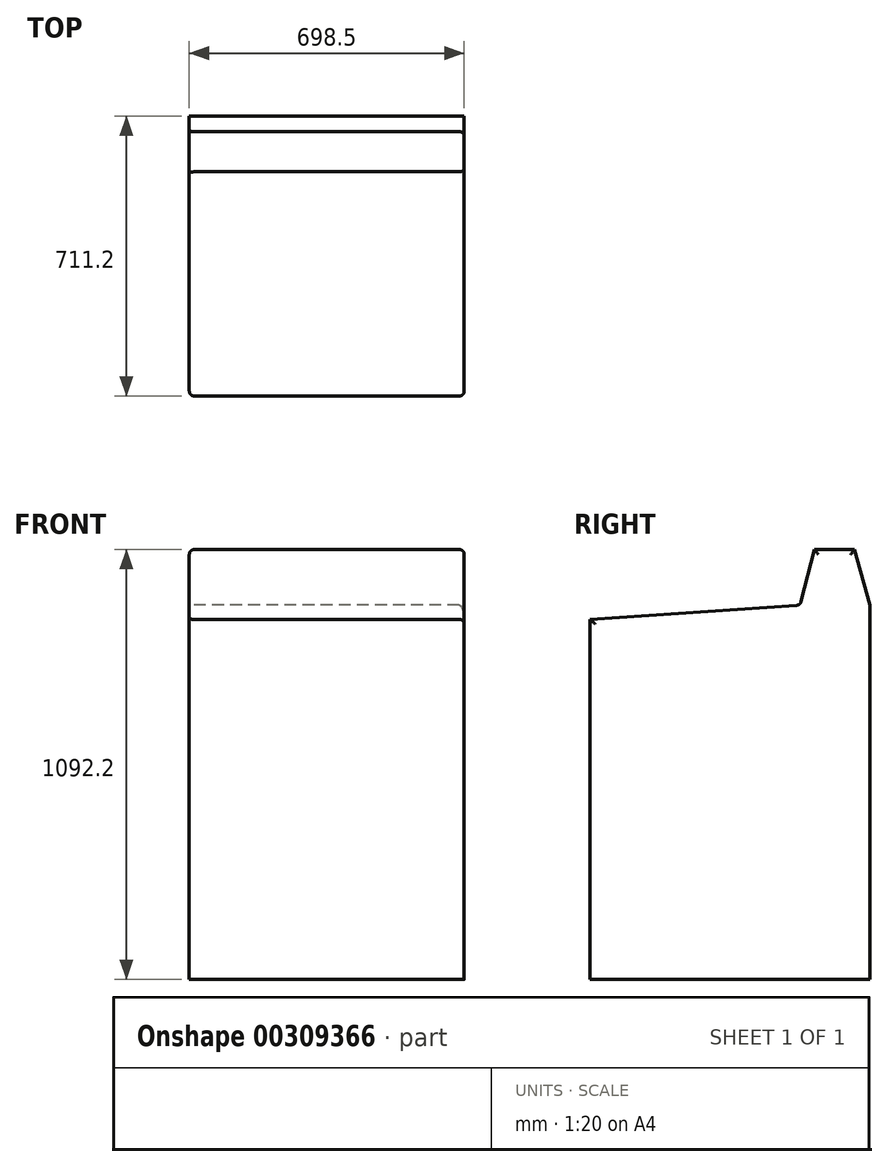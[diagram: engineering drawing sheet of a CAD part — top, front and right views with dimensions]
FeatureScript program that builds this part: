
annotation { "Feature Type Name" : "Feature", "Feature Type Description" : "" }
export const myFeature = defineFeature(function(context is Context, id is Id, definition is map)
    precondition{}
    {
        {
            var Q0;
            Q0=qCreatedBy(makeId("Top.planeOp"),FACE);
            var sketch = newSketch(context, id + "F0", { "sketchPlane" : qUnion([Q0])});
            skLineSegment(sketch, "E0.bottom", {"start": v(0, 0) * mm, "end": v(698.5, 0) * mm});
            skLineSegment(sketch, "E0.top", {"start": v(0, -711.2) * mm, "end": v(698.5, -711.2) * mm});
            skLineSegment(sketch, "E0.left", {"start": v(0, 0) * mm, "end": v(0, -711.2) * mm});
            skLineSegment(sketch, "E0.right", {"start": v(698.5, 0) * mm, "end": v(698.5, -711.2) * mm});
            skSolve(sketch);
        }
        {
            var Q0;
            Q0 = qSketchRegion(id + "F0", true);
            extrude(context, id + "F1", {"entities" : qUnion([Q0]), "depth" : 1092.2 * mm});
        }
        {
            var Q0;
            Q0=makeQuery(id+"F1.opExtrude","SWEPT_FACE",FACE,{"disambiguationData":[OSD([sQuery(id+"F0.wireOp",EDGE,"E0.left")])]});
            var sketch = newSketch(context, id + "F2", { "sketchPlane" : qUnion([Q0])});
            skLineSegment(sketch, "E1", {"start": v(0, 950.97) * mm, "end": v(39.62, 1092.2) * mm});
            skLineSegment(sketch, "E2", {"start": v(39.62, 1092.2) * mm, "end": v(141.55, 1092.2) * mm});
            skLineSegment(sketch, "E3", {"start": v(141.55, 1092.2) * mm, "end": v(177.52, 950.97) * mm});
            skLineSegment(sketch, "E4", {"start": v(177.52, 950.97) * mm, "end": v(711.2, 915) * mm});
            skSolve(sketch);
        }
        {
            var Q0;
            Q0 = qSketchRegion(id + "F2", true);
            var Q1;
            {var subQ0=sQuery(id+"F2.wireOp",EDGE,"E3");Q1=makeQuery(id+"F2.imprint","IMPRINT",FACE,{"disambiguationData":[TD([[makeQuery(id+"F2.imprint","IMPRINT",EDGE,{"derivedFrom":subQ0}),1.0]])]});}
            var Q2;
            {var subQ0=sQuery(id+"F2.wireOp",EDGE,"E1");Q2=makeQuery(id+"F2.imprint","IMPRINT",FACE,{"disambiguationData":[TD([[makeQuery(id+"F2.imprint","IMPRINT",EDGE,{"derivedFrom":subQ0}),1.0]])]});}
            extrude(context, id + "F3", {"entities" : qUnion([Q0, Q1, Q2]), "operationType" : NewBodyOperationType.REMOVE, "endBound" : BoundingType.THROUGH_ALL, "oppositeDirection" : true, "depth" : 25.4 * mm});
        }
        {
            var Q0;
            Q0=makeQuery(id+"F1.opExtrude","SWEPT_EDGE",EDGE,{"disambiguationData":[OSD([sQuery(id+"F0.wireOp",EDGE,"E0.top"),sQuery(id+"F0.wireOp",EDGE,"E0.left")])]});
            var Q1;
            Q1=makeQuery(id+"F1.opExtrude","SWEPT_EDGE",EDGE,{"disambiguationData":[OSD([sQuery(id+"F0.wireOp",EDGE,"E0.top"),sQuery(id+"F0.wireOp",EDGE,"E0.right")])]});
            var Q2;
            Q2=makeQuery(id+"F3.boolean.opBoolean","COPY",EDGE,{"derivedFrom":makeQuery(id+"F3.opExtrude","SWEPT_EDGE",EDGE,{"disambiguationData":[OSD([sQuery(id+"F0.wireOp",EDGE,"E0.top"),sQuery(id+"F0.wireOp",EDGE,"E0.left"),sQuery(id+"F2.wireOp",EDGE,"E4")])]})});
            var Q3;
            Q3=makeQuery(id+"F3.boolean.opBoolean","COPY",EDGE,{"derivedFrom":makeQuery(id+"F3.opExtrude","CAP_EDGE",EDGE,{"disambiguationData":[OSD([sQuery(id+"F2.wireOp",EDGE,"E4")])],"isStart":true})});
            var Q4;
            Q4=makeQuery(id+"F3.boolean.opBoolean","INTERSECT",EDGE,{"derivedFrom":[makeQuery(id+"F1.opExtrude","SWEPT_FACE",FACE,{"disambiguationData":[OSD([sQuery(id+"F0.wireOp",EDGE,"E0.right")])]}),makeQuery(id+"F3.opExtrude","SWEPT_FACE",FACE,{"disambiguationData":[OSD([sQuery(id+"F2.wireOp",EDGE,"E4")])]})]});
            var Q5;
            Q5=makeQuery(id+"F3.boolean.opBoolean","COPY",EDGE,{"derivedFrom":makeQuery(id+"F3.opExtrude","SWEPT_EDGE",EDGE,{"disambiguationData":[OSD([sQuery(id+"F2.wireOp",EDGE,"E3"),sQuery(id+"F2.wireOp",EDGE,"E4")])]})});
            var Q6;
            Q6=makeQuery(id+"F3.boolean.opBoolean","COPY",EDGE,{"derivedFrom":makeQuery(id+"F3.opExtrude","SWEPT_EDGE",EDGE,{"disambiguationData":[OSD([sQuery(id+"F0.wireOp",EDGE,"E0.left"),sQuery(id+"F2.wireOp",EDGE,"E2"),sQuery(id+"F2.wireOp",EDGE,"E3")])]})});
            var Q7;
            Q7=makeQuery(id+"F3.boolean.opBoolean","COPY",EDGE,{"derivedFrom":makeQuery(id+"F3.opExtrude","SWEPT_EDGE",EDGE,{"disambiguationData":[OSD([sQuery(id+"F0.wireOp",EDGE,"E0.left"),sQuery(id+"F2.wireOp",EDGE,"E1"),sQuery(id+"F2.wireOp",EDGE,"E2")])]})});
            var Q8;
            Q8=makeQuery(id+"F3.boolean.opBoolean","COPY",EDGE,{"derivedFrom":makeQuery(id+"F3.opExtrude","CAP_EDGE",EDGE,{"disambiguationData":[OSD([sQuery(id+"F2.wireOp",EDGE,"E3")])],"isStart":true})});
            var Q9;
            Q9=makeQuery(id+"F3.boolean.opBoolean","INTERSECT",EDGE,{"derivedFrom":[makeQuery(id+"F1.opExtrude","SWEPT_FACE",FACE,{"disambiguationData":[OSD([sQuery(id+"F0.wireOp",EDGE,"E0.right")])]}),makeQuery(id+"F3.opExtrude","SWEPT_FACE",FACE,{"disambiguationData":[OSD([sQuery(id+"F2.wireOp",EDGE,"E3")])]})]});
            var Q10;
            Q10=makeQuery(id+"F3.boolean.opBoolean","COPY",EDGE,{"derivedFrom":makeQuery(id+"F3.opExtrude","CAP_EDGE",EDGE,{"disambiguationData":[OSD([sQuery(id+"F2.wireOp",EDGE,"E1")])],"isStart":true})});
            var Q11;
            Q11=makeQuery(id+"F1.opExtrude","CAP_EDGE",EDGE,{"disambiguationData":[OSD([sQuery(id+"F0.wireOp",EDGE,"E0.right")])],"isStart":false});
            var Q12;
            Q12=makeQuery(id+"F3.boolean.opBoolean","INTERSECT",EDGE,{"derivedFrom":[makeQuery(id+"F1.opExtrude","SWEPT_FACE",FACE,{"disambiguationData":[OSD([sQuery(id+"F0.wireOp",EDGE,"E0.right")])]}),makeQuery(id+"F3.opExtrude","SWEPT_FACE",FACE,{"disambiguationData":[OSD([sQuery(id+"F2.wireOp",EDGE,"E1")])]})]});
            var Q13;
            Q13=makeQuery(id+"F1.opExtrude","CAP_EDGE",EDGE,{"disambiguationData":[OSD([sQuery(id+"F0.wireOp",EDGE,"E0.left")])],"isStart":false});
            fillet(context, id + "F4", {"entities" : qUnion([Q0, Q1, Q2, Q3, Q4, Q5, Q6, Q7, Q8, Q9, Q10, Q11, Q12, Q13]), "radius" : 12.7 * mm, "tangentPropagation" : true, "allowEdgeOverflow" : false});
        }
    });
